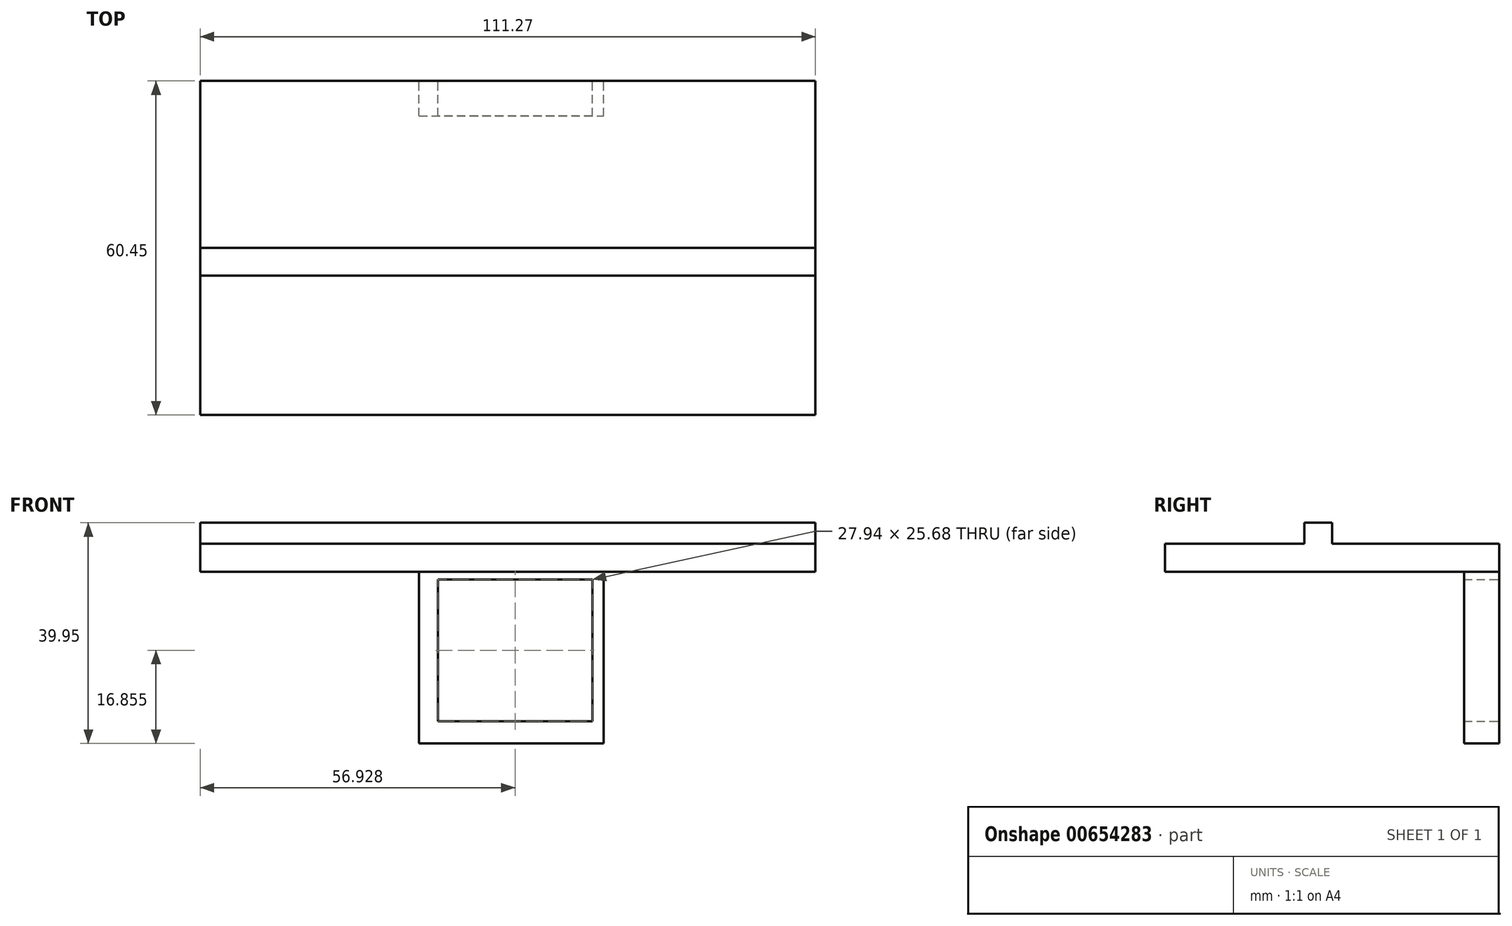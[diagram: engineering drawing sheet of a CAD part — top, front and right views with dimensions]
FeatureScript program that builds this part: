
annotation { "Feature Type Name" : "Feature", "Feature Type Description" : "" }
export const myFeature = defineFeature(function(context is Context, id is Id, definition is map)
    precondition{}
    {
        {
            var Q0;
            Q0=qCreatedBy(makeId("Front.planeOp"),FACE);
            var sketch = newSketch(context, id + "F0", { "sketchPlane" : qUnion([Q0])});
            skLineSegment(sketch, "E0", {"start": v(-55.94, 0) * mm, "end": v(55.33, 0) * mm});
            skLineSegment(sketch, "E1", {"start": v(55.33, 0) * mm, "end": v(55.33, 5.08) * mm});
            skLineSegment(sketch, "E2", {"start": v(55.33, 5.08) * mm, "end": v(-55.94, 5.08) * mm});
            skLineSegment(sketch, "E3", {"start": v(-55.94, 5.08) * mm, "end": v(-55.94, 0) * mm});
            skLineSegment(sketch, "E4.bottom", {"start": v(-16.38, 0) * mm, "end": v(17, 0) * mm});
            skLineSegment(sketch, "E4.top", {"start": v(-16.38, -31.06) * mm, "end": v(17, -31.06) * mm});
            skLineSegment(sketch, "E4.left", {"start": v(-16.38, 0) * mm, "end": v(-16.38, -31.06) * mm});
            skLineSegment(sketch, "E4.right", {"start": v(17, 0) * mm, "end": v(17, -31.06) * mm});
            skLineSegment(sketch, "E5", {"start": v(-12.98, -1.37) * mm, "end": v(-12.98, -27.04) * mm});
            skLineSegment(sketch, "E6", {"start": v(-12.98, -27.04) * mm, "end": v(14.96, -27.04) * mm});
            skLineSegment(sketch, "E7", {"start": v(14.96, -27.04) * mm, "end": v(14.96, -1.37) * mm});
            skLineSegment(sketch, "E8", {"start": v(14.96, -1.37) * mm, "end": v(-12.98, -1.37) * mm});
            skSolve(sketch);
        }
        {
            var Q0;
            Q0=makeQuery(id+"F0.imprint","IMPRINT",FACE,{"disambiguationData":[TD([[makeQuery(id+"F0.imprint","IMPRINT",EDGE,{"derivedFrom":sQuery(id+"F0.wireOp",EDGE,"E4.top")}),1.0]])]});
            extrude(context, id + "F1", {"entities" : qUnion([Q0]), "depth" : 6.35 * mm, "offsetDistance" : 25.4 * mm});
        }
        {
            var Q0;
            {var subQ0=sQuery(id+"F0.wireOp",EDGE,"E1");Q0=makeQuery(id+"F0.imprint","IMPRINT",FACE,{"disambiguationData":[TD([[makeQuery(id+"F0.imprint","IMPRINT",EDGE,{"derivedFrom":subQ0}),1.0]])]});}
            extrude(context, id + "F2", {"entities" : qUnion([Q0]), "operationType" : NewBodyOperationType.ADD, "depth" : 60.45 * mm, "offsetDistance" : 25.4 * mm});
        }
        {
            var Q0;
            Q0=makeQuery(id+"F2.opExtrude","SWEPT_FACE",FACE,{"disambiguationData":[OSD([sQuery(id+"F0.wireOp",EDGE,"E2")])]});
            var sketch = newSketch(context, id + "F3", { "sketchPlane" : qUnion([Q0])});
            skLineSegment(sketch, "E9.left", {"start": v(-55.94, -48.22) * mm, "end": v(-55.94, -51.35) * mm});
            skLineSegment(sketch, "E9.right", {"start": v(55.33, -48.22) * mm, "end": v(55.33, -51.35) * mm});
            skLineSegment(sketch, "E10.bottom", {"start": v(-55.94, -30.23) * mm, "end": v(55.33, -30.23) * mm});
            skLineSegment(sketch, "E10.top", {"start": v(-55.94, -35.21) * mm, "end": v(55.33, -35.21) * mm});
            skLineSegment(sketch, "E10.left", {"start": v(-55.94, -30.23) * mm, "end": v(-55.94, -35.21) * mm});
            skLineSegment(sketch, "E10.right", {"start": v(55.33, -30.23) * mm, "end": v(55.33, -35.21) * mm});
            skSolve(sketch);
        }
        {
            var Q0;
            Q0 = qSketchRegion(id + "F3", true);
            extrude(context, id + "F4", {"entities" : qUnion([Q0]), "operationType" : NewBodyOperationType.ADD, "depth" : 3.8 * mm, "offsetDistance" : 25.4 * mm});
        }
    });
